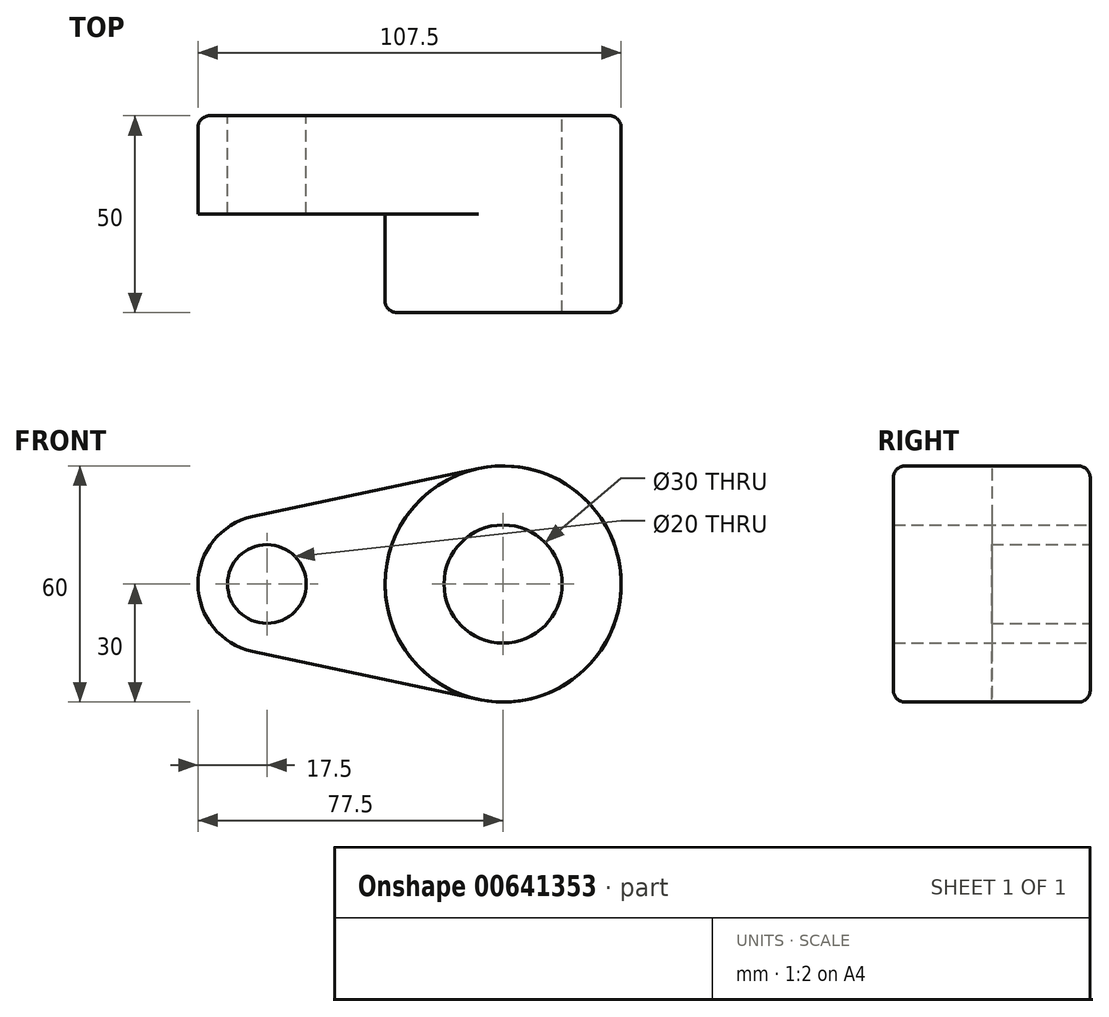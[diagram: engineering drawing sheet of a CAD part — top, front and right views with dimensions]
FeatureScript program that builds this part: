
annotation { "Feature Type Name" : "Feature", "Feature Type Description" : "" }
export const myFeature = defineFeature(function(context is Context, id is Id, definition is map)
    precondition{}
    {
        {
            var Q0;
            Q0=qCreatedBy(makeId("Front.planeOp"),FACE);
            var sketch = newSketch(context, id + "F0", { "sketchPlane" : qUnion([Q0])});
            skCircle(sketch, "E0", {"center": v(0, 0) * mm, "radius": 30 * mm});
            skCircle(sketch, "E1", {"center": v(-60, 0) * mm, "radius": 17.5 * mm});
            skLineSegment(sketch, "E2", {"start": v(-6.25, 29.34) * mm, "end": v(-63.65, 17.12) * mm});
            skLineSegment(sketch, "E3", {"start": v(-6.25, -29.34) * mm, "end": v(-63.65, -17.12) * mm});
            skCircle(sketch, "E4", {"center": v(-60, 0) * mm, "radius": 10 * mm});
            skCircle(sketch, "E5", {"center": v(0, 0) * mm, "radius": 15 * mm});
            skSolve(sketch);
        }
        {
            var Q0;
            Q0 = qSketchRegion(id + "F0", true);
            extrude(context, id + "F1", {"entities" : qUnion([Q0]), "depth" : 25 * mm, "offsetDistance" : 25 * mm});
        }
        {
            var Q0;
            Q0=makeQuery(id+"F0.imprint","IMPRINT",FACE,{"disambiguationData":[TD([[makeQuery(id+"F0.imprint","IMPRINT",EDGE,{"derivedFrom":sQuery(id+"F0.wireOp",EDGE,"E5")}),-1.0]])]});
            extrude(context, id + "F2", {"entities" : qUnion([Q0]), "operationType" : NewBodyOperationType.ADD, "depth" : 50 * mm, "offsetDistance" : 25 * mm});
        }
        {
            var Q0;
            Q0=makeQuery(id+"F2.opExtrude","CAP_EDGE",EDGE,{"disambiguationData":[OSD([sQuery(id+"F0.wireOp",EDGE,"E0")])],"isStart":false});
            var Q1;
            Q1=makeQuery(id+"F1.opExtrude","CAP_EDGE",EDGE,{"disambiguationData":[OSD([sQuery(id+"F0.wireOp",EDGE,"E0")])],"isStart":true});
            var Q2;
            Q2=makeQuery(id+"F1.opExtrude","CAP_EDGE",EDGE,{"disambiguationData":[OSD([sQuery(id+"F0.wireOp",EDGE,"E3")])],"isStart":true});
            var Q3;
            Q3=makeQuery(id+"F1.opExtrude","CAP_EDGE",EDGE,{"disambiguationData":[OSD([sQuery(id+"F0.wireOp",EDGE,"E1")])],"isStart":true});
            var Q4;
            Q4=makeQuery(id+"F1.opExtrude","CAP_EDGE",EDGE,{"disambiguationData":[OSD([sQuery(id+"F0.wireOp",EDGE,"E2")])],"isStart":true});
            fillet(context, id + "F3", {"entities" : qUnion([Q0, Q1, Q2, Q3, Q4]), "radius" : 3 * mm, "tangentPropagation" : true, "allowEdgeOverflow" : false});
        }
    });
